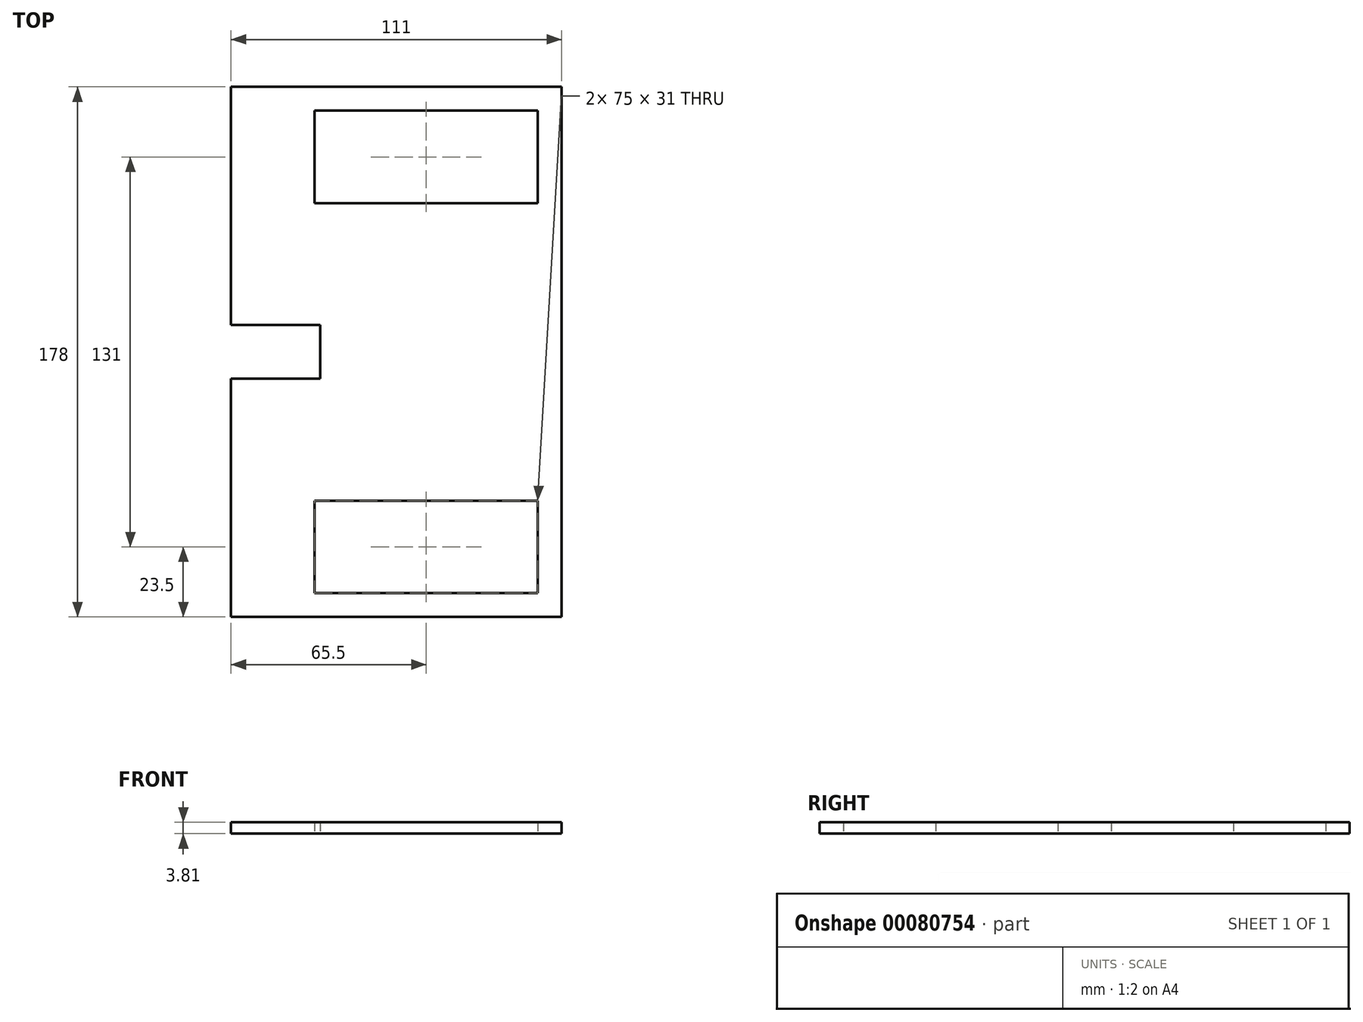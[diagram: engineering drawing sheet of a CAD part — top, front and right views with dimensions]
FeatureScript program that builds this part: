
annotation { "Feature Type Name" : "Feature", "Feature Type Description" : "" }
export const myFeature = defineFeature(function(context is Context, id is Id, definition is map)
    precondition{}
    {
        {
            var Q0;
            Q0=qCreatedBy(makeId("Top.planeOp"),FACE);
            var sketch = newSketch(context, id + "F0", { "sketchPlane" : qUnion([Q0])});
            skLineSegment(sketch, "E0.left", {"start": v(42.5, 89) * mm, "end": v(42.5, -89) * mm});
            skPoint(sketch, "E0.middle", {"position": v(0, 0) * mm});
            skLineSegment(sketch, "E1.bottom", {"start": v(34.5, 81) * mm, "end": v(-40.5, 81) * mm});
            skLineSegment(sketch, "E1.top", {"start": v(34.5, 50) * mm, "end": v(-40.5, 50) * mm});
            skLineSegment(sketch, "E1.left", {"start": v(34.5, 81) * mm, "end": v(34.5, 50) * mm});
            skLineSegment(sketch, "E1.right", {"start": v(-40.5, 81) * mm, "end": v(-40.5, 50) * mm});
            skPoint(sketch, "E1.middle", {"position": v(-3, 65.5) * mm});
            skLineSegment(sketch, "E2", {"start": v(-82.5, 0) * mm, "end": v(42.5, 0) * mm, "construction": true});
            skLineSegment(sketch, "E3.MirrorCS", {"start": v(-40.5, -81) * mm, "end": v(-40.5, -50) * mm});
            skLineSegment(sketch, "E4.MirrorCS", {"start": v(34.5, -81) * mm, "end": v(-40.5, -81) * mm});
            skLineSegment(sketch, "E5.MirrorCS", {"start": v(34.5, -81) * mm, "end": v(34.5, -50) * mm});
            skLineSegment(sketch, "E6.MirrorCS", {"start": v(34.5, -50) * mm, "end": v(-40.5, -50) * mm});
            skLineSegment(sketch, "E7", {"start": v(42.5, 79) * mm, "end": v(38.7, 79) * mm});
            skLineSegment(sketch, "E8", {"start": v(38.7, 79) * mm, "end": v(38.7, 64) * mm});
            skLineSegment(sketch, "E9", {"start": v(38.7, 64) * mm, "end": v(42.5, 64) * mm});
            skLineSegment(sketch, "E10", {"start": v(42.5, 54) * mm, "end": v(38.7, 54) * mm});
            skLineSegment(sketch, "E11", {"start": v(38.7, 54) * mm, "end": v(38.7, 39) * mm});
            skLineSegment(sketch, "E12", {"start": v(38.7, 39) * mm, "end": v(42.5, 39) * mm});
            skLineSegment(sketch, "E13.MirrorCS", {"start": v(38.7, -39) * mm, "end": v(42.5, -39) * mm});
            skLineSegment(sketch, "E14.MirrorCS", {"start": v(38.7, -54) * mm, "end": v(38.7, -39) * mm});
            skLineSegment(sketch, "E15.MirrorCS", {"start": v(42.5, -54) * mm, "end": v(38.7, -54) * mm});
            skLineSegment(sketch, "E16.MirrorCS", {"start": v(38.7, -64) * mm, "end": v(42.5, -64) * mm});
            skLineSegment(sketch, "E17.MirrorCS", {"start": v(38.7, -79) * mm, "end": v(38.7, -64) * mm});
            skLineSegment(sketch, "E18.MirrorCS", {"start": v(42.5, -79) * mm, "end": v(38.7, -79) * mm});
            skLineSegment(sketch, "E19", {"start": v(-68.5, -85.19) * mm, "end": v(-68.5, -89) * mm});
            skLineSegment(sketch, "E20.MirrorCS", {"start": v(-68.5, 85.19) * mm, "end": v(-68.5, 89) * mm});
            skLineSegment(sketch, "E21", {"start": v(-68.5, 89) * mm, "end": v(-68.5, -89) * mm});
            skLineSegment(sketch, "E22", {"start": v(-68.5, 89) * mm, "end": v(42.5, 89) * mm});
            skLineSegment(sketch, "E23", {"start": v(-68.5, -89) * mm, "end": v(42.5, -89) * mm});
            skLineSegment(sketch, "E24", {"start": v(-38.5, -9) * mm, "end": v(-68.5, -9) * mm});
            skLineSegment(sketch, "E25", {"start": v(-38.5, -9) * mm, "end": v(-38.5, 0) * mm});
            skLineSegment(sketch, "E26.MirrorCS", {"start": v(-38.5, 9) * mm, "end": v(-38.5, 0) * mm});
            skLineSegment(sketch, "E27.MirrorCS", {"start": v(-38.5, 9) * mm, "end": v(-68.5, 9) * mm});
            skSolve(sketch);
        }
        {
            var Q0;
            Q0=makeQuery(id+"F0.imprint","IMPRINT",FACE,{"disambiguationData":[TD([[makeQuery(id+"F0.imprint","IMPRINT",EDGE,{"derivedFrom":sQuery(id+"F0.wireOp",EDGE,"E1.bottom")}),-1.0]])]});
            var Q1;
            {var subQ0=sQuery(id+"F0.wireOp",EDGE,"E7");Q1=makeQuery(id+"F0.imprint","IMPRINT",FACE,{"disambiguationData":[TD([[makeQuery(id+"F0.imprint","IMPRINT",EDGE,{"derivedFrom":subQ0}),1.0]])]});}
            var Q2;
            {var subQ0=sQuery(id+"F0.wireOp",EDGE,"E10");Q2=makeQuery(id+"F0.imprint","IMPRINT",FACE,{"disambiguationData":[TD([[makeQuery(id+"F0.imprint","IMPRINT",EDGE,{"derivedFrom":subQ0}),1.0]])]});}
            var Q3;
            {var subQ0=sQuery(id+"F0.wireOp",EDGE,"E13.MirrorCS");Q3=makeQuery(id+"F0.imprint","IMPRINT",FACE,{"disambiguationData":[TD([[makeQuery(id+"F0.imprint","IMPRINT",EDGE,{"derivedFrom":subQ0}),-1.0]])]});}
            var Q4;
            {var subQ0=sQuery(id+"F0.wireOp",EDGE,"E16.MirrorCS");Q4=makeQuery(id+"F0.imprint","IMPRINT",FACE,{"disambiguationData":[TD([[makeQuery(id+"F0.imprint","IMPRINT",EDGE,{"derivedFrom":subQ0}),-1.0]])]});}
            extrude(context, id + "F1", {"entities" : qUnion([Q0, Q1, Q2, Q3, Q4]), "depth" : 3.8 * mm});
        }
    });
